# Revit family: Cabinet bed Tobi unfolded
name_source: partatom
category: Casework
revit_build: Autodesk Revit MEP 2013 (Build: 20120221_2030(x64)
units: mm (PartAtom-declared; Revit-internal decimal feet)

## types (1)
- Cabinet bed Tobi unfolded
    BIMobject Category = Furniture
    BIMobject QR code url = http://vaneritarvike.bimobject.com
    Back Panel Material = Valkoinen
    Bed Bottom Side Panel Material = koivu
    Bed Legs Material = koivu
    Bed Material = Ma_tpatja
    Bed Top Side Panel Material = koivu
    Bottom Bed Material = koivu
    Bottom Panel Material = Valkoinen
    Date of publishing = 4/2/2013
    Depth = 1800 mm  [stored 5.90551 ft]
    Design country = Finland
    Door Material = Valkoinen
    Edition number = 2
    Handle Material = Valkoinen
    Height = 2300 mm
    IFC Classification = Furniture
    Legs Support Material = koivu
    Manufacture country = Finland
    Manufacturer = Nokian Vaneritarvike Oy
    Manufacturer URL = http://www.vaneritarvike.fi
    Model = Cabinet bed Tobi unfolded
    Name of the object = Cabinet bed Tobi unfolded
    Product SKU = 7530
    Product data url = http://www.vaneritarvike.fi
    Product family = Kindergarten Furniture
    Product group = Cabinet bed
    Side Panel Material = Valkoinen
    Top Panel Material = Valkoinen
    UNSPC Category = Furniture and Furnishings
    UNSPC code = 56
    URL = http://vaneritarvike.bimobject.com
    Weight Net (kg) = 0 mm  [stored 0 ft]
    Width = 700 mm  [stored 2.29659 ft]

note: [stored X ft] marks values corroborated as IEEE doubles in the binary element streams (Revit-internal decimal feet)

## geometry (parser evidence)
native form markers: Blend x92, Sweep x2
no freeform markers — native parametric forms only
